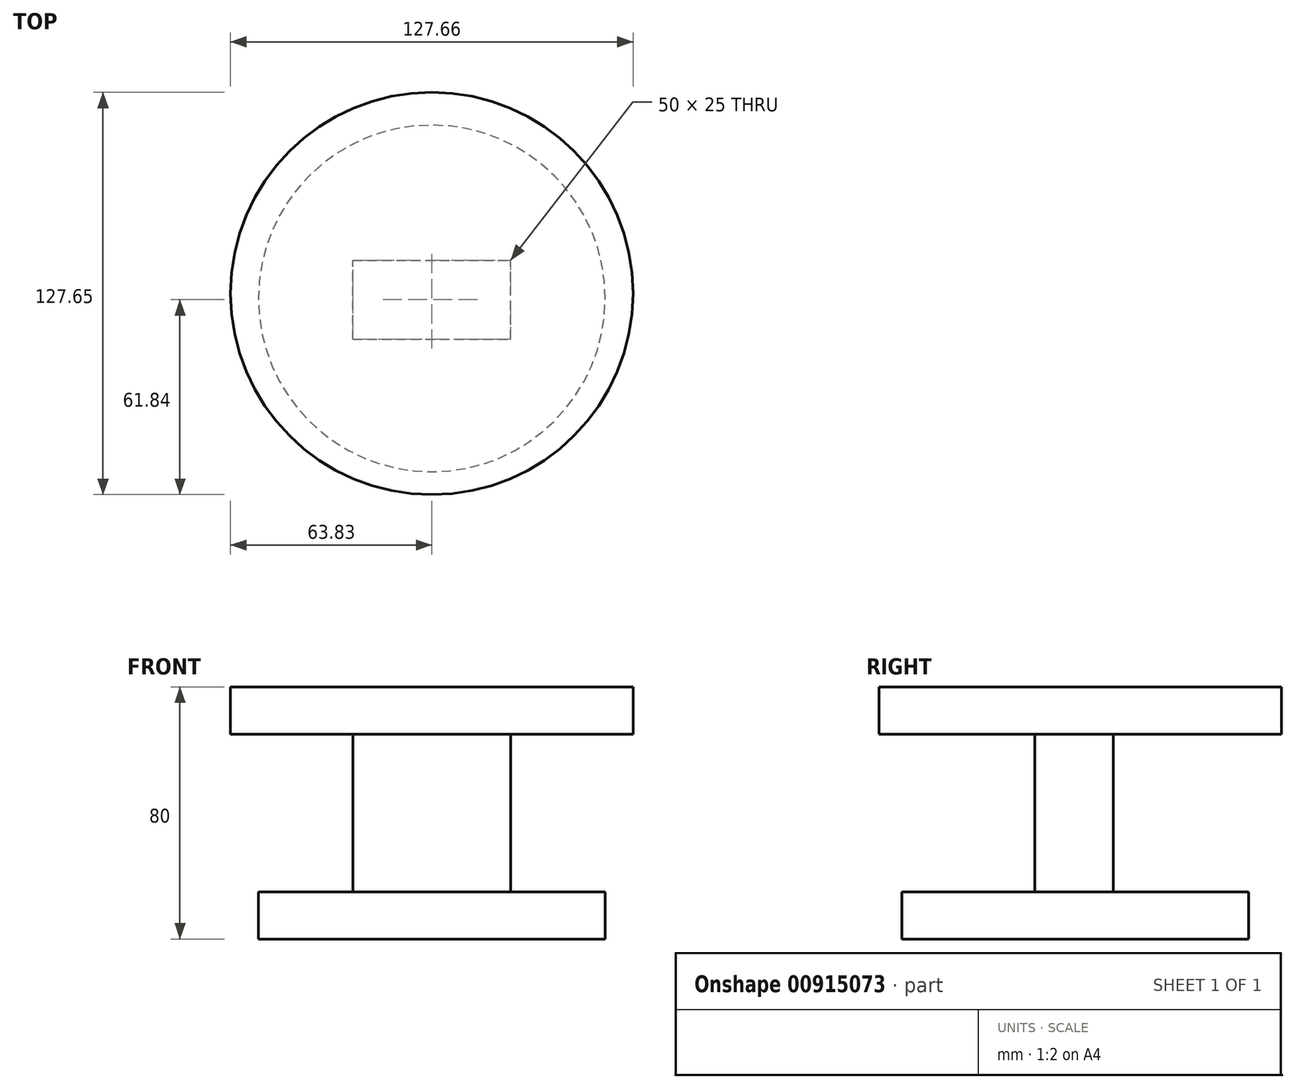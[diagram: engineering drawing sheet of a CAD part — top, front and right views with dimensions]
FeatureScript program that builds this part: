
annotation { "Feature Type Name" : "Feature", "Feature Type Description" : "" }
export const myFeature = defineFeature(function(context is Context, id is Id, definition is map)
    precondition{}
    {
        {
            var Q0;
            Q0=qCreatedBy(makeId("Front.planeOp"),FACE);
            var sketch = newSketch(context, id + "F0", { "sketchPlane" : qUnion([Q0])});
            skLineSegment(sketch, "E0.bottom", {"start": v(-25, 25) * mm, "end": v(25, 25) * mm});
            skLineSegment(sketch, "E0.top", {"start": v(-25, -25) * mm, "end": v(25, -25) * mm});
            skLineSegment(sketch, "E0.left", {"start": v(-25, 25) * mm, "end": v(-25, -25) * mm});
            skLineSegment(sketch, "E0.right", {"start": v(25, 25) * mm, "end": v(25, -25) * mm});
            skPoint(sketch, "E0.middle", {"position": v(0, 0) * mm});
            skSolve(sketch);
        }
        {
            var Q0;
            Q0 = qSketchRegion(id + "F0", true);
            var Q1;
            Q1=makeQuery(id+"F0.imprint","IMPRINT",FACE,{"disambiguationData":[TD([[makeQuery(id+"F0.imprint","IMPRINT",EDGE,{"derivedFrom":sQuery(id+"F0.wireOp",EDGE,"E0.bottom")}),-1.0]])]});
            extrude(context, id + "F1", {"entities" : qUnion([Q0, Q1]), "depth" : 25 * mm, "offsetDistance" : 25 * mm});
        }
        {
            var Q0;
            Q0=makeQuery(id+"F1.opExtrude","SWEPT_FACE",FACE,{"disambiguationData":[OSD([sQuery(id+"F0.wireOp",EDGE,"E0.bottom")])]});
            var sketch = newSketch(context, id + "F2", { "sketchPlane" : qUnion([Q0])});
            skCircle(sketch, "E1", {"center": v(0, -10.51) * mm, "radius": 63.83 * mm});
            skSolve(sketch);
        }
        {
            var Q0;
            Q0 = qSketchRegion(id + "F2", true);
            extrude(context, id + "F3", {"entities" : qUnion([Q0]), "operationType" : NewBodyOperationType.ADD, "depth" : 15 * mm, "offsetDistance" : 25 * mm});
        }
        {
            var Q0;
            Q0=makeQuery(id+"F1.opExtrude","SWEPT_FACE",FACE,{"disambiguationData":[OSD([sQuery(id+"F0.wireOp",EDGE,"E0.top")])]});
            var sketch = newSketch(context, id + "F4", { "sketchPlane" : qUnion([Q0])});
            skCircle(sketch, "E2", {"center": v(0, 12.1) * mm, "radius": 54.99 * mm});
            skSolve(sketch);
        }
        {
            var Q0;
            Q0=makeQuery(id+"F1.opExtrude","SWEPT_FACE",FACE,{"disambiguationData":[OSD([sQuery(id+"F0.wireOp",EDGE,"E0.top")])]});
            var Q1;
            Q1=makeQuery(id+"F4.imprint","IMPRINT",FACE,{"disambiguationData":[TD([[makeQuery(id+"F4.imprint","IMPRINT",EDGE,{"derivedFrom":sQuery(id+"F4.wireOp",EDGE,"E2")}),1.0]])]});
            var Q2;
            {var subQ0=sQuery(id+"F0.wireOp",EDGE,"E0.top");Q2=makeQuery(id+"F4.imprint","IMPRINT",FACE,{"disambiguationData":[TD([[makeQuery(id+"F4.imprint","IMPRINT",EDGE,{"derivedFrom":makeQuery(id+"F1.opExtrude","CAP_EDGE",EDGE,{"disambiguationData":[OSD([subQ0])],"isStart":true})}),1.0]])]});}
            extrude(context, id + "F5", {"entities" : qUnion([Q0, Q1, Q2]), "operationType" : NewBodyOperationType.ADD, "depth" : 15 * mm, "offsetDistance" : 25 * mm});
        }
    });
